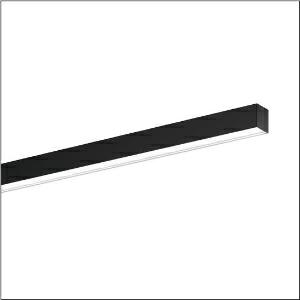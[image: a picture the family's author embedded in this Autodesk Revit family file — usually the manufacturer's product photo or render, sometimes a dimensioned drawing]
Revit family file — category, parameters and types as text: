
# Revit family: silica_r__21_51mx23dc3abb_3531
name_source: partatom
category: Lighting Fixtures
units: mm (PartAtom-declared; Revit-internal decimal feet)

## family parameters
Cut with Voids When Loaded = No
Host = Face
Light Source = No
Part Type = Normal
Room Calculation Point = No
Round Connector Dimension = Use Diameter
Shared = No

## types (1)
- --- (1 x LED, 8200 lm, 62.2 W, 3000K)
    Apparent Load = 62 VA
    CIE Flux Codes = 78 96 99 100 100
    Color Rendering = 80
    Color Temperature = 3000K
    Default Elevation = 1800 mm
    Description = Silica® 21, office luminaire, primary optical cover: prismatic diffuser, of PMMA, CAT 2 (L<= 3000cd/m²), light emission: direct distribution, primary light characteristic: symmetric, installation type: surface-mounted, LED, rated luminous flux: 8.200lm, luminous efficacy: 132lm/W, light colour: 830, colour temperature: 3000K, with terminal, 3+2-pole, max. 2.5mm², mains connection: 220..240V, AC, 50/60Hz, rated input power: 62.2W, luminaire housing, of aluminium, jet black (RAL 9005), length: 3.004mm, width: 53mm, height: 53mm, protection rating (complete): IP20, insulation class (complete): insulation class I (protective earthing), certification: CE, permissible operating ambient temperature: 0..+35°C, standard: EN 50419, packaging unit: 1 piece
    Height = 0 mm  [stored 0 ft]
    Lamp = 1 x LED
    Lamp Light Flux = 8200 lm
    Lamp Power = 62.2 W
    Lamp count = 1
    Length = 3004 mm
    Luminous efficacy = 132 lm/W
    Manufacturer = Siteco
    ModVariant = No
    Model = 51MX23DC3ABB
    Mounting Place = Ceiling
    Mounting Type = Recessed
    Number of Poles = 1
    OnlyDefault = Yes
    Power Factor = 1
    Product Name = Silica® 21
    Product group = office luminaire | ceiling recessed
    ProductGroupID = 401
    Protection Class = Protection class I
    Protection Degree = IP 20
    RLX_Detail_Level = 1
    RLX_Emergency_Light_Flux = 0 lm
    RLX_Emergency_Type = 0
    RLX_Emergency_Type_DB = No
    RlxData = <blob elided: 23649 chars, md5=9f068a5b>
    Socket = socket
    Standby Power = 0 W
    System Light Flux = 8200 lm
    System Power = 62 W
    Type Comments = factory setting: luminous flux: 100 % | dim-lin: 254 | 345 mA
    Type Image = l_1297760.jpg
    URL = http://relux.com
    VarID = @adj_049823
    Voltage = 0 V
    Weight = 0.00 kg
    Width = 53 mm

note: [stored X ft] marks values corroborated as IEEE doubles in the binary element streams (Revit-internal decimal feet)

## geometry (parser evidence)
native form markers: Blend x4, Sweep x11
no freeform markers — native parametric forms only
